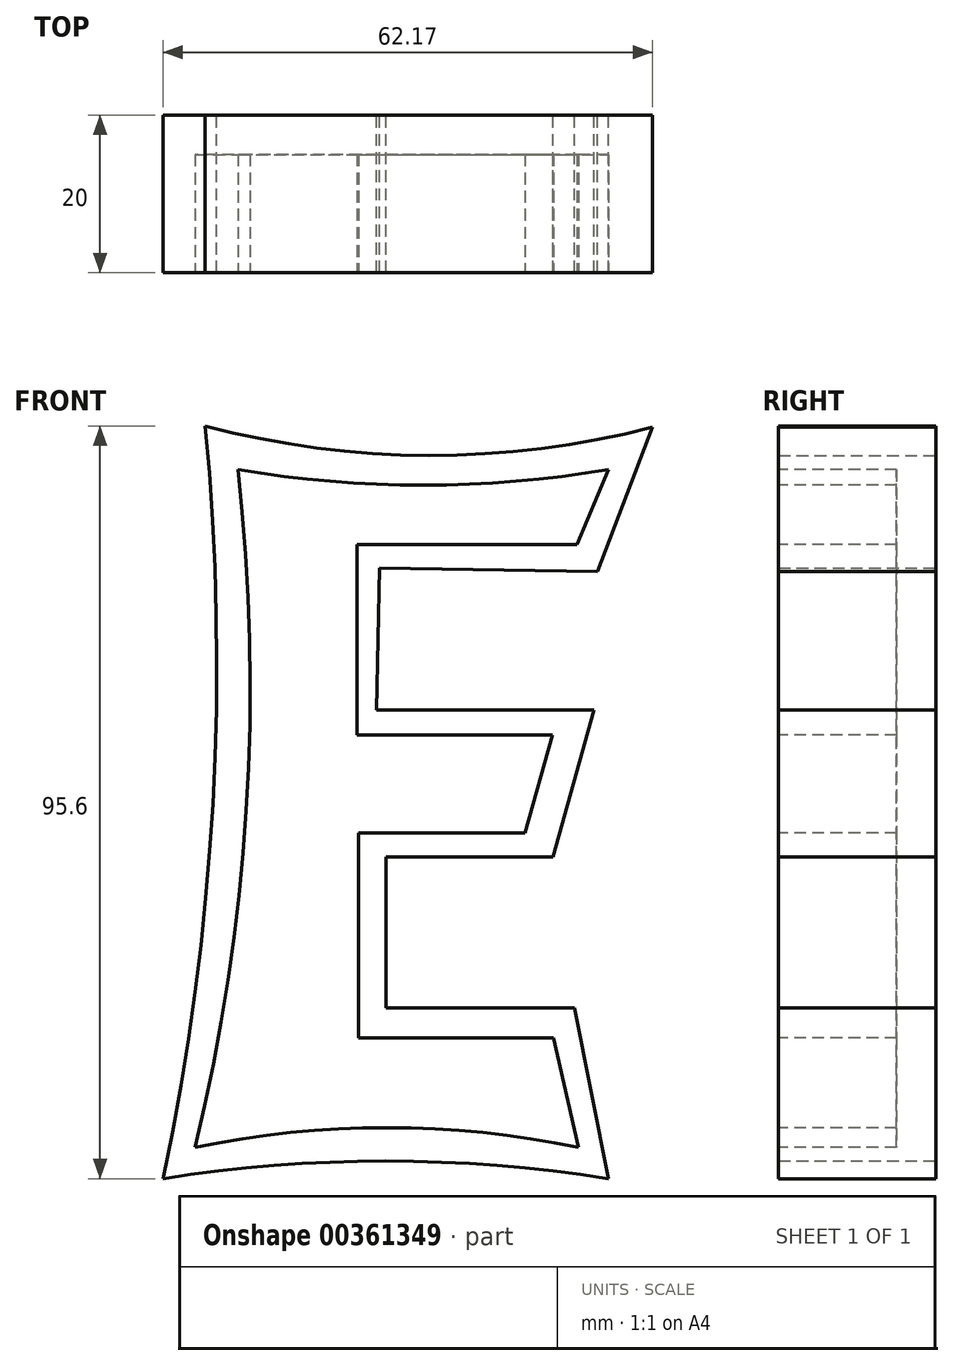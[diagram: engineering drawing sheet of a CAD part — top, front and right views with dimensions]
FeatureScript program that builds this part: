
annotation { "Feature Type Name" : "Feature", "Feature Type Description" : "" }
export const myFeature = defineFeature(function(context is Context, id is Id, definition is map)
    precondition{}
    {
        {
            var Q0;
            Q0=qCreatedBy(makeId("Front.planeOp"),FACE);
            var sketch = newSketch(context, id + "F0", { "sketchPlane" : qUnion([Q0])});
            skArc(sketch, "E0", {"start": v(-27.97, -49.77) * mm, "mid": v(-21.65, -2.17) * mm, "end": v(-22.61, 45.83) * mm});
            skArc(sketch, "E1", {"start": v(28.58, -49.77) * mm, "mid": v(0.3, -47.53) * mm, "end": v(-27.97, -49.77) * mm});
            skArc(sketch, "E2", {"start": v(-22.61, 45.83) * mm, "mid": v(5.78, 42.11) * mm, "end": v(34.2, 45.69) * mm});
            skLineSegment(sketch, "E3", {"start": v(34.2, 45.69) * mm, "end": v(27.22, 27.35) * mm});
            skLineSegment(sketch, "E4", {"start": v(27.22, 27.35) * mm, "end": v(-0.49, 27.81) * mm});
            skLineSegment(sketch, "E5", {"start": v(26.8, 9.76) * mm, "end": v(21.58, -8.89) * mm});
            skLineSegment(sketch, "E6", {"start": v(21.58, -8.89) * mm, "end": v(0.34, -8.89) * mm});
            skLineSegment(sketch, "E7", {"start": v(0.34, -8.89) * mm, "end": v(0.34, -28.07) * mm});
            skLineSegment(sketch, "E8", {"start": v(0.34, -28.07) * mm, "end": v(24.32, -28.07) * mm});
            skLineSegment(sketch, "E9", {"start": v(24.32, -28.07) * mm, "end": v(28.58, -49.77) * mm});
            skLineSegment(sketch, "E10", {"start": v(26.8, 9.76) * mm, "end": v(-0.87, 9.78) * mm});
            skLineSegment(sketch, "E11", {"start": v(-0.49, 27.81) * mm, "end": v(-0.87, 9.78) * mm});
            skSolve(sketch);
        }
        {
            var Q0;
            Q0 = qSketchRegion(id + "F0", true);
            extrude(context, id + "F1", {"entities" : qUnion([Q0]), "depth" : 20 * mm});
        }
        {
            var Q0;
            Q0=makeQuery(id+"F1.opExtrude","CAP_FACE",FACE,{"disambiguationData":[OSD([sQuery(id+"F0.wireOp",EDGE,"E0"),sQuery(id+"F0.wireOp",EDGE,"E1"),sQuery(id+"F0.wireOp",EDGE,"E2"),sQuery(id+"F0.wireOp",EDGE,"E3"),sQuery(id+"F0.wireOp",EDGE,"E4"),sQuery(id+"F0.wireOp",EDGE,"E5"),sQuery(id+"F0.wireOp",EDGE,"E6"),sQuery(id+"F0.wireOp",EDGE,"E7"),sQuery(id+"F0.wireOp",EDGE,"E8"),sQuery(id+"F0.wireOp",EDGE,"E9"),sQuery(id+"F0.wireOp",EDGE,"E10"),sQuery(id+"F0.wireOp",EDGE,"E11")])],"isStart":false});
            var sketch = newSketch(context, id + "F2", { "sketchPlane" : qUnion([Q0])});
            skArc(sketch, "E12", {"start": v(-23.9, -45.79) * mm, "mid": v(-17.4, -2.98) * mm, "end": v(-18.47, 40.3) * mm});
            skArc(sketch, "E13", {"start": v(24.77, -45.79) * mm, "mid": v(0.44, -43.3) * mm, "end": v(-23.9, -45.79) * mm});
            skArc(sketch, "E14", {"start": v(-18.47, 40.3) * mm, "mid": v(5.06, 38.34) * mm, "end": v(28.58, 40.3) * mm});
            skLineSegment(sketch, "E15", {"start": v(28.58, 40.3) * mm, "end": v(24.63, 30.79) * mm});
            skLineSegment(sketch, "E16", {"start": v(24.63, 30.79) * mm, "end": v(-3.34, 30.79) * mm});
            skLineSegment(sketch, "E17", {"start": v(-3.34, 30.79) * mm, "end": v(-3.34, 6.57) * mm});
            skLineSegment(sketch, "E18", {"start": v(-3.34, 6.57) * mm, "end": v(21.48, 6.57) * mm});
            skLineSegment(sketch, "E19", {"start": v(21.48, 6.57) * mm, "end": v(17.99, -5.84) * mm});
            skLineSegment(sketch, "E20", {"start": v(17.99, -5.84) * mm, "end": v(-3.15, -5.84) * mm});
            skLineSegment(sketch, "E21", {"start": v(-3.15, -5.84) * mm, "end": v(-3.15, -31.87) * mm});
            skLineSegment(sketch, "E22", {"start": v(-3.15, -31.87) * mm, "end": v(21.61, -31.87) * mm});
            skLineSegment(sketch, "E23", {"start": v(21.61, -31.87) * mm, "end": v(24.77, -45.79) * mm});
            skSolve(sketch);
        }
        {
            var Q0;
            Q0 = qSketchRegion(id + "F2", true);
            extrude(context, id + "F3", {"entities" : qUnion([Q0]), "operationType" : NewBodyOperationType.REMOVE, "oppositeDirection" : true, "depth" : 15 * mm});
        }
    });
